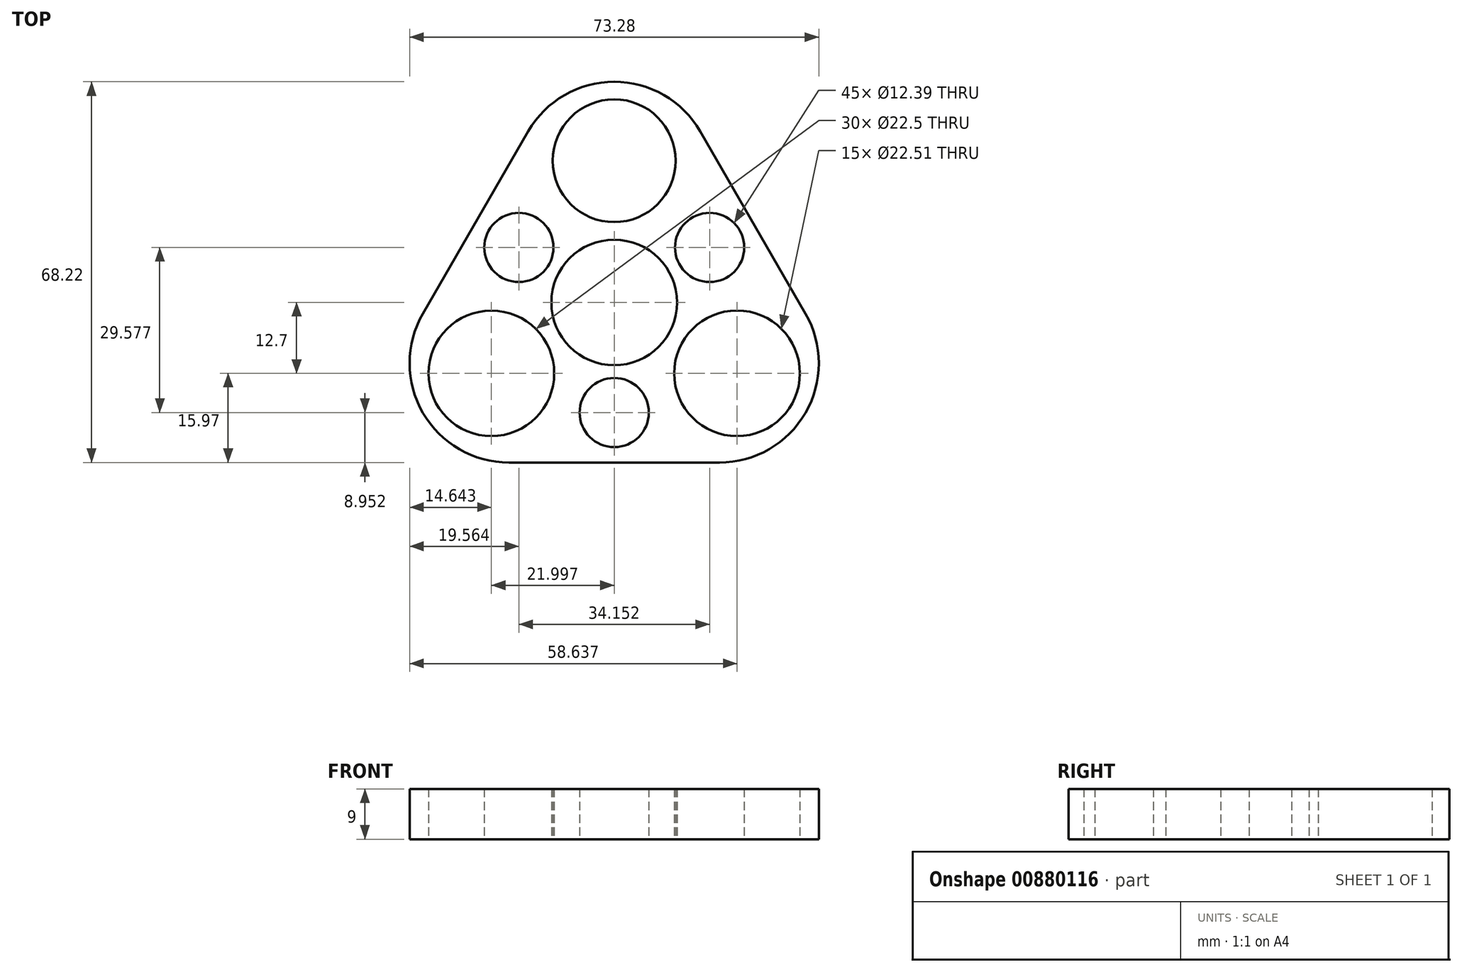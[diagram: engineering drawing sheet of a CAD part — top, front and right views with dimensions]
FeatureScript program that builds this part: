
annotation { "Feature Type Name" : "Feature", "Feature Type Description" : "" }
export const myFeature = defineFeature(function(context is Context, id is Id, definition is map)
    precondition{}
    {
        {
            var Q0;
            Q0=qCreatedBy(makeId("Top.planeOp"),FACE);
            var sketch = newSketch(context, id + "F0", { "sketchPlane" : qUnion([Q0])});
            skCircle(sketch, "E0", {"center": v(0, 0) * mm, "radius": 11.25 * mm});
            skCircle(sketch, "E1", {"center": v(0, 25.4) * mm, "radius": 11 * mm});
            skPoint(sketch, "E2.0.midPoint", {"position": v(0, -25.4) * mm});
            skLineSegment(sketch, "E3", {"start": v(0, 0) * mm, "end": v(-44, -25.4) * mm, "construction": true});
            skLineSegment(sketch, "E4", {"start": v(0, 0) * mm, "end": v(44, -25.4) * mm, "construction": true});
            skCircle(sketch, "E5", {"center": v(-22, -12.7) * mm, "radius": 11.25 * mm});
            skCircle(sketch, "E6", {"center": v(22, -12.7) * mm, "radius": 11.26 * mm});
            skLineSegment(sketch, "E7", {"start": v(-22, -12.7) * mm, "end": v(-22, -35.49) * mm, "construction": true});
            skLineSegment(sketch, "E8", {"start": v(22, -12.7) * mm, "end": v(22, -37.52) * mm, "construction": true});
            skLineSegment(sketch, "E9.anchor1", {"start": v(0, 0) * mm, "end": v(-22, -24.1) * mm, "construction": true});
            skCircle(sketch, "E10.cCircle", {"center": v(0, 0) * mm, "radius": 28.67 * mm, "construction": true});
            skLineSegment(sketch, "E10.0", {"start": v(18.86, -28.67) * mm, "end": v(-18.86, -28.67) * mm});
            skLineSegment(sketch, "E10.1", {"start": v(-34.26, -2) * mm, "end": v(-15.4, 30.66) * mm});
            skLineSegment(sketch, "E10.2", {"start": v(15.4, 30.66) * mm, "end": v(34.26, -2) * mm});
            skPoint(sketch, "E10.0.midPoint", {"position": v(0, -28.67) * mm});
            skPoint(sketch, "E11.visualSharp", {"position": v(-49.65, -28.67) * mm});
            skArc(sketch, "E11.filletArc", {"start": v(-34.26, -2) * mm, "mid": v(-34.26, -19.78) * mm, "end": v(-18.86, -28.67) * mm});
            skPoint(sketch, "E12.visualSharp", {"position": v(49.65, -28.67) * mm});
            skArc(sketch, "E12.filletArc", {"start": v(18.86, -28.67) * mm, "mid": v(34.26, -19.78) * mm, "end": v(34.26, -2) * mm});
            skPoint(sketch, "E13.visualSharp", {"position": v(0, 57.33) * mm});
            skArc(sketch, "E13.filletArc", {"start": v(15.4, 30.66) * mm, "mid": v(0, 39.55) * mm, "end": v(-15.4, 30.66) * mm});
            skCircle(sketch, "E14", {"center": v(-17.08, 9.86) * mm, "radius": 6.2 * mm});
            skLineSegment(sketch, "E15", {"start": v(0, 0) * mm, "end": v(-43.05, 24.85) * mm, "construction": true});
            skCircle(sketch, "E16.1.0", {"center": v(0, -19.72) * mm, "radius": 6.2 * mm});
            skCircle(sketch, "E16.2.0", {"center": v(17.08, 9.86) * mm, "radius": 6.2 * mm});
            skSolve(sketch);
        }
        {
            var Q0;
            Q0=makeQuery(id+"F0.imprint","IMPRINT",FACE,{"disambiguationData":[TD([[makeQuery(id+"F0.imprint","IMPRINT",EDGE,{"derivedFrom":sQuery(id+"F0.wireOp",EDGE,"E0")}),-1.0]])]});
            extrude(context, id + "F1", {"entities" : qUnion([Q0]), "depth" : 9 * mm, "offsetDistance" : 25.4 * mm});
        }
    });
